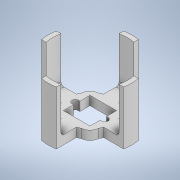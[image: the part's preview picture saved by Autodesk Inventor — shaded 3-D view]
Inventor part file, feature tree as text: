
AUTODESK INVENTOR PART (.ipt)
format: ipt  version: 2020 (Build 240168000, 168)  size: 246,784 bytes
history: native  units: mm
features: extrude x3, sketch x2, other x1, fillet x1, projected_geometry x1
ambient origin geometry x8: Origin, YZ Plane, XZ Plane, XY Plane, X Axis, Y Axis, Z Axis, Center Point
bodies: Body1 (feature_tree)
feature tree (8):
  other  "Твердое тело1"
  sketch  "Эскиз1"
  extrude  "Выдавливание1"  Depth=17.8mm
  extrude  "Выдавливание2"  Depth=17.8mm
  extrude  "Выдавливание3"  Depth=1.8mm
  fillet  "Сопряжение1"  Radius=20.0mm
  sketch  "Эскиз2"
  projected_geometry  "Спроецированная петля1"
